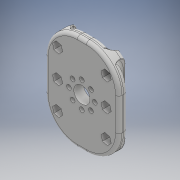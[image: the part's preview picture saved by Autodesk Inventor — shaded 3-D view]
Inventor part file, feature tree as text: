
AUTODESK INVENTOR PART (.ipt)
format: ipt  version: 2018 (Build 220112000, 112)  size: 1,396,224 bytes
history: native  units: mm
features: fillet x4, extrude x3, sketch x2, projected_geometry x1
ambient origin geometry x8: Origin, YZ Plane, XZ Plane, XY Plane, X Axis, Y Axis, Z Axis, Center Point
bodies: Solid1 (feature_tree)
feature tree (10):
  sketch  "Sketch1"  dims[d0=2.0mm d1=2.0mm]
  extrude  "Extrusion1"  Depth=2.0mm
  extrude  "Extrusion2"  Depth=5.6mm
  fillet  "Fillet1"  Radius=6.0mm
  fillet  "Fillet2"  Radius=4.0mm
  fillet  "Fillet3"  Radius=20.0mm
  fillet  "Fillet4"  Radius=3.0mm
  extrude  "Extrusion3"  Depth=5.6mm
  sketch  "Sketch2"  dims[d2=2.0mm d3=2.0mm d5=80.0mm d6=1.0mm d7=10.0mm d8=16.0mm d9=2.9mm d10=360.0deg d11=6.0mm d12=0.0mm d13=4.0mm d14=0.0mm d15=20.0mm d16=3.0mm d17=2.0mm d18=0.5mm d19=5.6mm d20=6.0mm d21=0.0mm d22=5.6mm d23=5.6mm d24=5.6mm d25=5.6mm d26=5.6mm]
  projected_geometry  "Projected Loop2"
